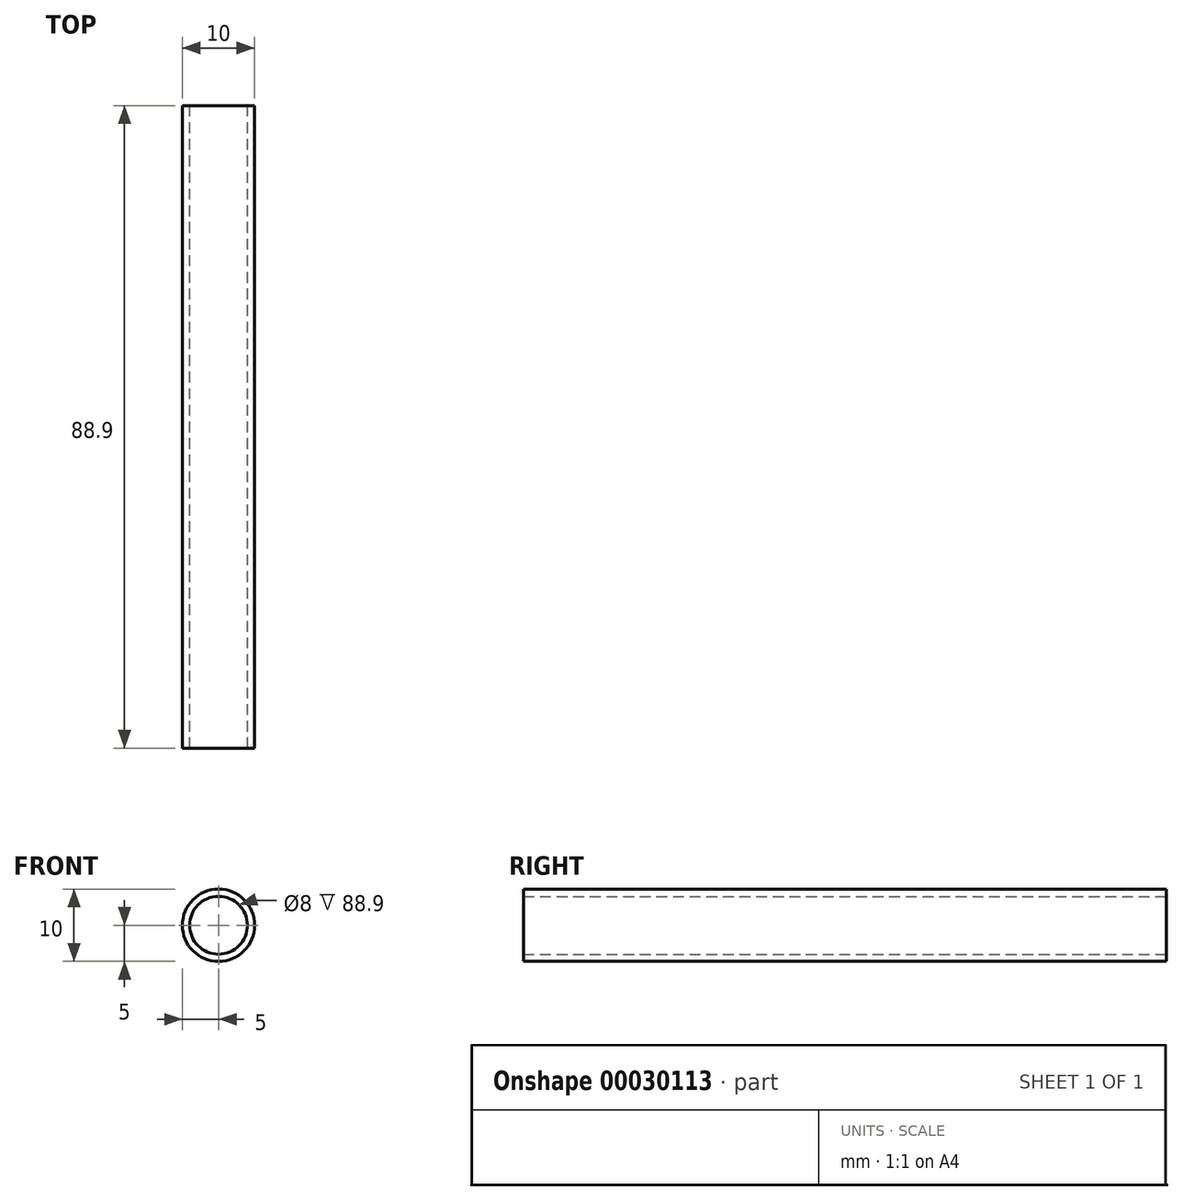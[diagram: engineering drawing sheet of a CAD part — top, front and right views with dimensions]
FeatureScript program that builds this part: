
annotation { "Feature Type Name" : "Feature", "Feature Type Description" : "" }
export const myFeature = defineFeature(function(context is Context, id is Id, definition is map)
    precondition{}
    {
        {
            var Q0;
            Q0=qCreatedBy(makeId("Front.planeOp"),FACE);
            var sketch = newSketch(context, id + "F0", { "sketchPlane" : qUnion([Q0])});
            skCircle(sketch, "E0", {"center": v(0, 0) * mm, "radius": 5 * mm});
            skCircle(sketch, "E1", {"center": v(0, 0) * mm, "radius": 4 * mm});
            skSolve(sketch);
        }
        {
            var Q0;
            Q0 = qSketchRegion(id + "F0", true);
            extrude(context, id + "F1", {"entities" : qUnion([Q0]), "depth" : 88.9 * mm});
        }
    });
